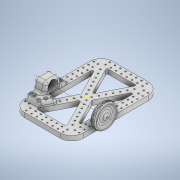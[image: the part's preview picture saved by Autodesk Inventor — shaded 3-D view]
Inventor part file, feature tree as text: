
AUTODESK INVENTOR PART (.ipt)
format: ipt  version: 2021 (Build 250183000, 183)  size: 2,037,760 bytes
history: native  units: mm
features: sketch x20, extrude x13, other x9, fillet x8, hole x4, pattern_linear x3, mirror x3, plane x2, pattern_circular x1, revolve x1
ambient origin geometry x8: Origin, YZ Plane, XZ Plane, XY Plane, X Axis, Y Axis, Z Axis, Center Point
bodies: Body1 (feature_tree), Body2 (feature_tree), Body3 (feature_tree), Body4 (feature_tree)
feature tree (64):
  other  "Chassis"
  extrude  "Extrusion1"  Depth=50.0mm
  fillet  "Fillet1"  Radius=9.0mm
  fillet  "Fillet2"  Radius=9.0mm
  sketch  "Sketch4"  dims[d18=9.0mm]
  hole  "Hole1"  [1 undecoded]
  pattern_linear  "Rectangular Pattern1"  Count1=2  [1 undecoded]
  sketch  "Sketch5"  dims[d19=9.0mm]
  hole  "Hole2"  [1 undecoded]
  pattern_linear  "Rectangular Pattern2"  Count1=2 Spacing1=7.0mm
  hole  "Hole3"  [1 undecoded]
  pattern_linear  "Rectangular Pattern3"  Count1=7 Spacing1=9.0mm
  mirror  "Mirror1"
  mirror  "Mirror2"
  extrude  "Extrusion2"  Depth=75.0mm
  extrude  "Extrusion4"  Depth=15.0mm
  extrude  "Extrusion5"  Depth=15.0mm
  extrude  "Extrusion6"  Depth=8.90625mm
  extrude  "Extrusion7"  Depth=10.0mm
  extrude  "Extrusion9"  Depth=2.0mm
  hole  "Hole5"  [1 undecoded]
  fillet  "Fillet3"  Radius=13.0mm
  fillet  "Fillet4"  Radius=20.0mm
  mirror  "Mirror3"
  extrude  "Extrusion10"  Depth=2.0mm TaperAngle=0.0deg
  extrude  "Extrusion11"  Depth=2.0mm
  extrude  "Extrusion13"  Depth=2.0mm TaperAngle=0.0deg
  extrude  "Extrusion15"  Depth=2.0mm
  extrude  "Extrusion16"  Depth=10.0mm
  fillet  "Fillet10"  Radius=12.0mm
  fillet  "Fillet11"  Radius=12.0mm
  fillet  "Fillet12"  Radius=18.0mm
  fillet  "Fillet13"  Radius=6.1mm
  other  "Work Point2"
  plane  "Work Plane1"
  extrude  "Extrusion17"  Depth=2.0mm TaperAngle=0.0deg
  pattern_circular  "Circular Pattern1"  Count=6  [1 undecoded]
  other  "Work Axis3"
  other  "Work Point3"
  plane  "Work Plane3"
  revolve  "Revolution1"  [1 undecoded]
  sketch  "Sketch1"  dims[d2=50.0mm d3=50.0mm d14=9.0mm d15=9.0mm]
  sketch  "Sketch3"  dims[d16=9.0mm d17=9.0mm]
  sketch  "Sketch6"  dims[d20=9.0mm]
  sketch  "Sketch7"  dims[d27=8.0mm d28=0.0mm]
  sketch  "Sketch8"  dims[d29=2.0mm d30=20.0mm]
  other  "Wheel Block Right"
  sketch  "Sketch10"  dims[d210=2.459mm d211=6.0mm d212=4.0mm d213=2.0mm d214=90.0deg d215=8.8mm d216=20.594885mm d219=40.0mm d221=-9.0mm]
  sketch  "Sketch11"  dims[d223=4.0mm]
  sketch  "Sketch12"  dims[d224=2.459mm d225=6.0mm d226=4.0mm d227=2.0mm d228=90.0deg d229=8.8mm d230=20.594885mm]
  sketch  "Sketch13"  dims[d231=4.5mm]
  sketch  "Sketch16"  dims[d232=4.0mm d233=20.0mm d235=7.0mm d236=4.5mm]
  sketch  "Sketch17"  dims[d237=70.0mm d239=9.0mm d240=20.0mm d242=7.0mm d243=4.5mm]
  other  "Pattern of Wheel Block Right:1"
  other  "Wheel Block Left"
  sketch  "Sketch18"  dims[d245=4.5mm]
  other  "Wheel"
  sketch  "Sketch19"  dims[d247=2.459mm d248=6.0mm d249=4.0mm d250=2.0mm d251=90.0deg d252=8.0mm d253=20.594885mm d254=70.0mm d256=9.0mm]
  sketch  "Sketch21"  dims[d257=75.0mm d258=75.0mm]
  sketch  "Sketch23"  dims[d259=15.0mm d260=15.0mm]
  sketch  "Sketch24"  dims[d261=15.0mm d262=15.0mm]
  sketch  "Sketch25"  dims[d263=9.0mm d264=8.90625mm]
  other  "Work Axis1"
  sketch  "Sketch28"  dims[d269=10.0mm d270=10.0mm d271=4.0mm d272=25.0mm d273=24.0mm d274=13.0mm d275=13.0mm d285=20.0mm d286=0.0mm d294=14.0mm d295=0.0mm d296=17.0mm d297=110.75mm d298=0.0mm d299=17.0mm d300=10.0mm d301=12.0mm d302=12.0mm d303=18.0mm d304=0.0mm d305=6.1mm d306=18.0mm d307=0.0mm d319=60.0mm d320=2.0mm d321=5.0mm d323=8.0mm d324=30.0mm d325=8.0mm d326=5.0mm d327=24.0mm d328=18.0mm d329=0.0mm d330=0.0mm d331=0.0mm d332=0.0mm d333=0.0mm d334=0.0mm d335=0.0mm d336=0.0mm d337=0.0mm d338=0.0mm d339=0.0mm d340=0.0mm d341=0.0mm d342=0.0mm d343=0.0mm d344=3.2mm d345=6.0mm d346=6.3mm d347=2.0mm d348=90.0deg d349=8.0mm d350=20.594885mm d351=25.0mm d352=25.0mm d353=5.0mm d354=2.0mm d355=12.0mm d356=0.0mm d357=40.0mm d358=10.0mm d359=0.0mm d371=1.5mm d372=4.0mm d373=0.0mm d374=8.0mm d375=0.0mm d380=3.0mm d381=2.0mm d382=3.5mm d383=0.0mm d384=0.0mm d385=0.0mm d386=3.5mm d387=0.0mm d388=5.0mm d389=5.0mm d390=5.0mm d391=1.0mm d401=1.0mm d402=-0.349066mm d403=400.0mm d404=360.0deg d427=0.2mm d428=0.2mm d429=0.4mm d430=0.4mm d432=1.5mm d433=2.5mm d434=1.0mm d435=1.0mm d436=1.752523mm d441=1.0mm d442=0.4175mm d443=0.417349mm d444=0.2mm d445=90.0deg]
note: 7 required parameter values undecoded (feature->parameter linkage not recoverable at this tier; creation-order binding heuristic only, values carry confidence <= 0.55)